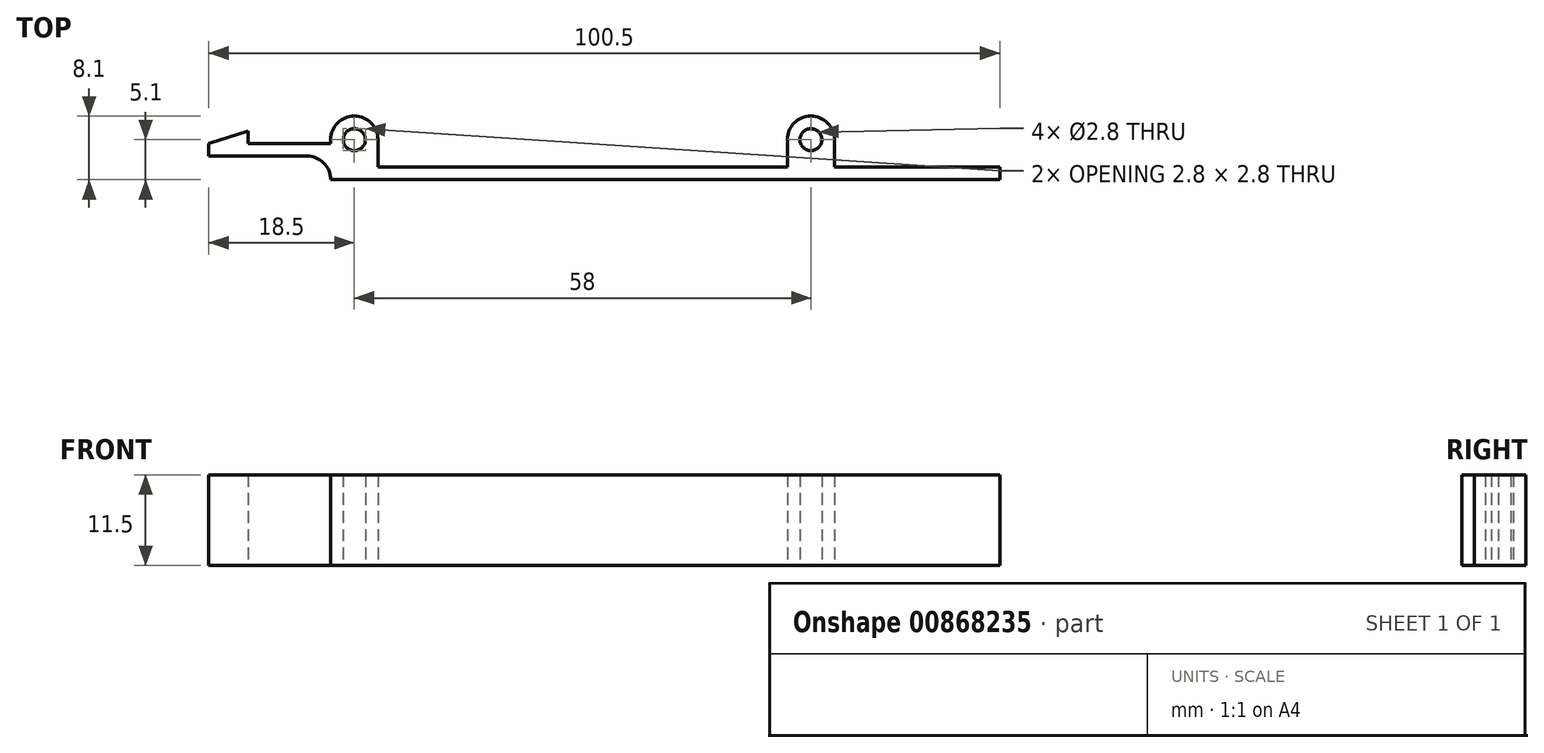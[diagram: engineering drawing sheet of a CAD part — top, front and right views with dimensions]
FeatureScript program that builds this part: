
annotation { "Feature Type Name" : "Feature", "Feature Type Description" : "" }
export const myFeature = defineFeature(function(context is Context, id is Id, definition is map)
    precondition{}
    {
        {
            var Q0;
            Q0=qCreatedBy(makeId("Top.planeOp"),FACE);
            var sketch = newSketch(context, id + "F0", { "sketchPlane" : qUnion([Q0])});
            skLineSegment(sketch, "E0", {"start": v(24, -5.1) * mm, "end": v(-61, -5.1) * mm});
            skLineSegment(sketch, "E1", {"start": v(3, -3.5) * mm, "end": v(3, 0) * mm});
            skArc(sketch, "E2", {"start": v(-3, 0) * mm, "mid": v(0, 3) * mm, "end": v(3, 0) * mm});
            skLineSegment(sketch, "E3", {"start": v(-3, 0) * mm, "end": v(-3, -3.5) * mm});
            skLineSegment(sketch, "E4", {"start": v(24, -3.5) * mm, "end": v(24, -5.1) * mm});
            skLineSegment(sketch, "E5", {"start": v(-61, -5.1) * mm, "end": v(-61, -2.1) * mm});
            skLineSegment(sketch, "E6", {"start": v(-61, -2.1) * mm, "end": v(-76.5, -2.1) * mm});
            skLineSegment(sketch, "E7", {"start": v(-76.5, -2.1) * mm, "end": v(-76.5, -0.5) * mm});
            skLineSegment(sketch, "E8", {"start": v(-76.5, -0.5) * mm, "end": v(-71.5, 1.1) * mm});
            skLineSegment(sketch, "E9", {"start": v(-71.5, 1.1) * mm, "end": v(-71.5, -0.5) * mm});
            skLineSegment(sketch, "E10", {"start": v(-71.5, -0.5) * mm, "end": v(-76.5, -0.5) * mm, "construction": true});
            skLineSegment(sketch, "E11", {"start": v(-71.5, -0.5) * mm, "end": v(-61, -0.5) * mm});
            skLineSegment(sketch, "E12", {"start": v(-61, -0.5) * mm, "end": v(-61, 0) * mm});
            skLineSegment(sketch, "E13", {"start": v(-55, -3.5) * mm, "end": v(-55, 0) * mm});
            skLineSegment(sketch, "E14", {"start": v(-55, 0) * mm, "end": v(-61, 0) * mm, "construction": true});
            skArc(sketch, "E15", {"start": v(-55, 0) * mm, "mid": v(-58, 3) * mm, "end": v(-61, 0) * mm});
            skLineSegment(sketch, "E16", {"start": v(-61, -0.5) * mm, "end": v(-61, -2.1) * mm, "construction": true});
            skLineSegment(sketch, "E17", {"start": v(24, -3.5) * mm, "end": v(3, -3.5) * mm});
            skLineSegment(sketch, "E18", {"start": v(-3, -3.5) * mm, "end": v(-55, -3.5) * mm});
            skLineSegment(sketch, "E19", {"start": v(-3, -3.5) * mm, "end": v(3, -3.5) * mm, "construction": true});
            skSolve(sketch);
        }
        {
            var Q0;
            Q0 = qSketchRegion(id + "F0", true);
            extrude(context, id + "F1", {"entities" : qUnion([Q0]), "depth" : 11.5 * mm, "offsetDistance" : 25 * mm});
        }
        {
            var Q0;
            Q0=sQuery(id+"F0.wireOp",VERTEX,"E15.center");
            var Q1;
            Q1=sQuery(id+"F0.wireOp",VERTEX,"E2.center");
            var Q2;
            Q2=makeQuery(id+"F1.opExtrude","SWEPT_BODY",BODY,{"disambiguationData":[OSD([sQuery(id+"F0.wireOp",EDGE,"E0"),sQuery(id+"F0.wireOp",EDGE,"RVtHzhuv-uF1o-i02D-Tj21-tROGK15kUXmW"),sQuery(id+"F0.wireOp",EDGE,"wcJamsxY-RlFf-VI1T-zocU-VqVn2BVgQjx3"),sQuery(id+"F0.wireOp",EDGE,"m4YN4zhr-vtQg-Y5eq-boOb-jyr9xo5xEpfn"),sQuery(id+"F0.wireOp",EDGE,"MQIm2Lo3-R5J6-oLGU-iQXr-DQy6LmfbWCVx"),sQuery(id+"F0.wireOp",EDGE,"cgOxu6z8-tZpU-c0us-SLWr-rv0e0sqg2c3t"),sQuery(id+"F0.wireOp",EDGE,"wC359uLM-xTXe-dJYJ-DVDH-QwBqN2sTC0Ce"),sQuery(id+"F0.wireOp",EDGE,"FlWom4P7-5wcy-a2wN-odAo-HupqPnAKDR2o"),sQuery(id+"F0.wireOp",EDGE,"njYXQObc-1leY-I912-3XWT-fgJbyTMMmanq"),sQuery(id+"F0.wireOp",EDGE,"E1"),sQuery(id+"F0.wireOp",EDGE,"E2"),sQuery(id+"F0.wireOp",EDGE,"E3"),sQuery(id+"F0.wireOp",EDGE,"tfPguPok-lrYH-ZT1z-WARM-It2NTSy56bQx"),sQuery(id+"F0.wireOp",EDGE,"E4")])]});
            hole(context, id + "F2", {"style" : HoleStyle.SIMPLE, "endStyle" : HoleEndStyle.THROUGH, "oppositeDirection" : true, "holeDiameter" : 2.8 * mm, "majorDiameter" : 5 * mm, "isTappedThrough" : true, "tappedDepth" : 12 * mm, "tapClearance" : 3, "locations" : qUnion([Q0, Q1]), "scope" : qUnion([Q2])});
        }
        {
            var Q0;
            Q0=makeQuery(id+"F1.opExtrude","SWEPT_EDGE",EDGE,{"disambiguationData":[OSD([sQuery(id+"F0.wireOp",EDGE,"E5"),sQuery(id+"F0.wireOp",EDGE,"E6")])]});
            fillet(context, id + "F3", {"entities" : qUnion([Q0]), "radius" : 3 * mm, "tangentPropagation" : true, "allowEdgeOverflow" : false});
        }
    });
